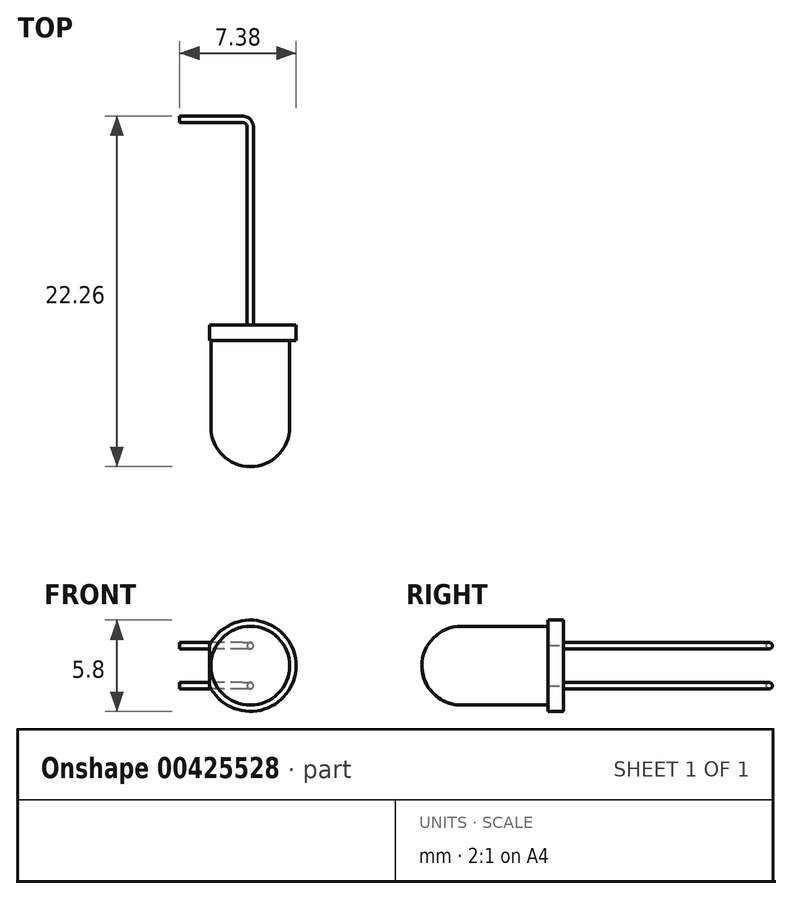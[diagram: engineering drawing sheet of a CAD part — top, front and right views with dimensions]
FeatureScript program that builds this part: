
annotation { "Feature Type Name" : "Feature", "Feature Type Description" : "" }
export const myFeature = defineFeature(function(context is Context, id is Id, definition is map)
    precondition{}
    {
        {
            var Q0;
            Q0=qCreatedBy(makeId("Front.planeOp"),FACE);
            var sketch = newSketch(context, id + "F0", { "sketchPlane" : qUnion([Q0])});
            skArc(sketch, "E0.0", {"start": v(-2.6, 1.28) * mm, "mid": v(2.9, 0) * mm, "end": v(-2.6, -1.28) * mm});
            skLineSegment(sketch, "E1", {"start": v(-2.6, -1.28) * mm, "end": v(-2.6, 1.28) * mm});
            skSolve(sketch);
        }
        {
            var Q0;
            Q0 = qSketchRegion(id + "F0", true);
            extrude(context, id + "F1", {"entities" : qUnion([Q0]), "depth" : 1 * mm});
        }
        {
            var Q0;
            Q0=qCreatedBy(makeId("Top.planeOp"),FACE);
            var sketch = newSketch(context, id + "F2", { "sketchPlane" : qUnion([Q0])});
            skLineSegment(sketch, "E2", {"start": v(0, 0) * mm, "end": v(0, 12.56) * mm});
            skLineSegment(sketch, "E3", {"start": v(-0.5, 13.06) * mm, "end": v(-4.48, 13.06) * mm});
            skPoint(sketch, "E4.visualSharp", {"position": v(0, 13.06) * mm});
            skArc(sketch, "E4.filletArc", {"start": v(0, 12.56) * mm, "mid": v(-0.15, 12.9) * mm, "end": v(-0.5, 13.06) * mm});
            skSolve(sketch);
        }
        {
            var Q0;
            Q0=qCreatedBy(makeId("Front.planeOp"),FACE);
            var sketch = newSketch(context, id + "F3", { "sketchPlane" : qUnion([Q0])});
            skCircle(sketch, "E5", {"center": v(0, 1.27) * mm, "radius": 0.2 * mm});
            skCircle(sketch, "E6.MirrorC", {"center": v(0, -1.27) * mm, "radius": 0.2 * mm});
            skSolve(sketch);
        }
        {
            var Q0;
            Q0=qSketchRegion(id+"F3",true);
            var Q1;
            Q1=qConstructionFilter(qBodyType(qCreatedBy(id+"F2",EDGE),BodyType.WIRE),ConstructionObject.NO);
            sweep(context, id + "F4", {"operationType" : NewBodyOperationType.ADD, "profiles" : qUnion([Q0]), "path" : qUnion([Q1])});
        }
        {
            var Q0;
            Q0=makeQuery(id+"F1.opExtrude","CAP_FACE",FACE,{"disambiguationData":[OSD([sQuery(id+"F0.wireOp",EDGE,"E0.0"),sQuery(id+"F0.wireOp",EDGE,"E1")])],"isStart":false});
            var sketch = newSketch(context, id + "F5", { "sketchPlane" : qUnion([Q0])});
            skCircle(sketch, "E7", {"center": v(0, 0) * mm, "radius": 2.5 * mm});
            skSolve(sketch);
        }
        {
            var Q0;
            Q0 = qSketchRegion(id + "F5", true);
            extrude(context, id + "F6", {"entities" : qUnion([Q0]), "operationType" : NewBodyOperationType.ADD, "depth" : 8 * mm});
        }
        {
            var Q0;
            Q0=makeQuery(id+"F6.opExtrude","CAP_EDGE",EDGE,{"disambiguationData":[OSD([sQuery(id+"F5.wireOp",EDGE,"E7")])],"isStart":false});
            fillet(context, id + "F7", {"entities" : qUnion([Q0]), "radius" : 2.5 * mm, "tangentPropagation" : true, "allowEdgeOverflow" : false});
        }
    });
